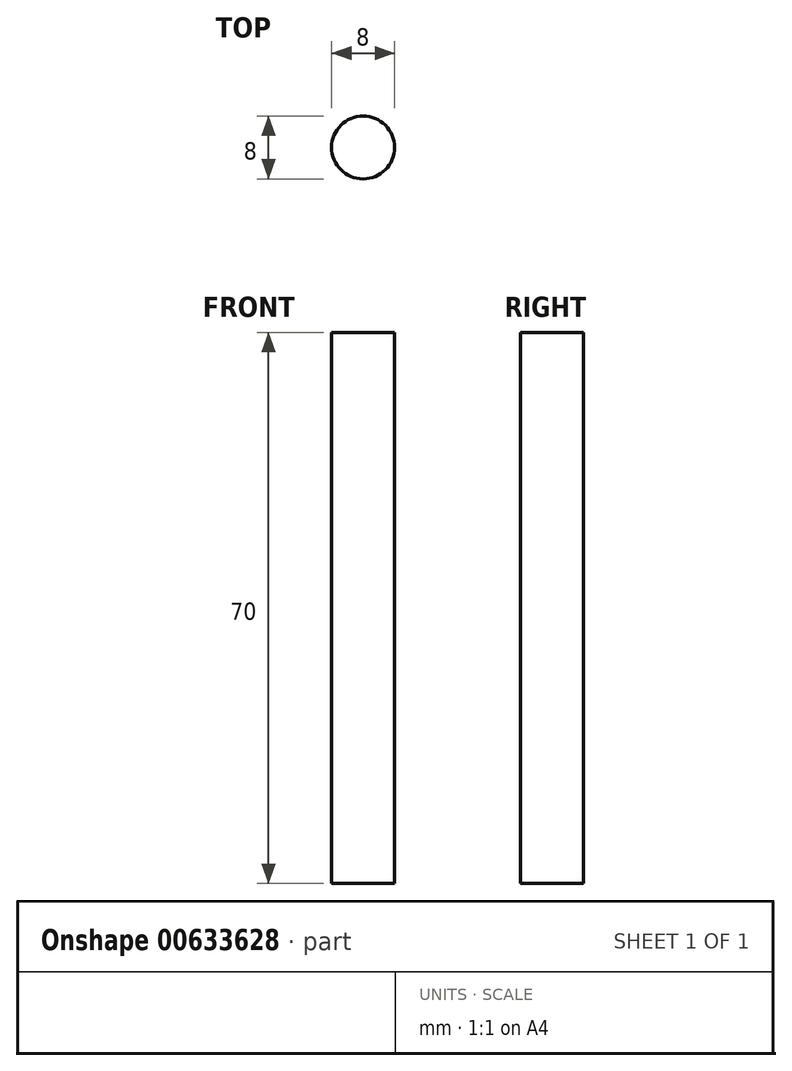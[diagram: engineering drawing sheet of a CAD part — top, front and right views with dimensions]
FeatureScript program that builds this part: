
annotation { "Feature Type Name" : "Feature", "Feature Type Description" : "" }
export const myFeature = defineFeature(function(context is Context, id is Id, definition is map)
    precondition{}
    {
        {
            var Q0;
            Q0=qCreatedBy(makeId("Top.planeOp"),FACE);
            var sketch = newSketch(context, id + "F0", { "sketchPlane" : qUnion([Q0])});
            skCircle(sketch, "E0", {"center": v(0, 0) * mm, "radius": 4 * mm});
            skSolve(sketch);
        }
        {
            var Q0;
            Q0 = qSketchRegion(id + "F0", true);
            extrude(context, id + "F1", {"entities" : qUnion([Q0]), "depth" : 70 * mm, "offsetDistance" : 25 * mm});
        }
    });
